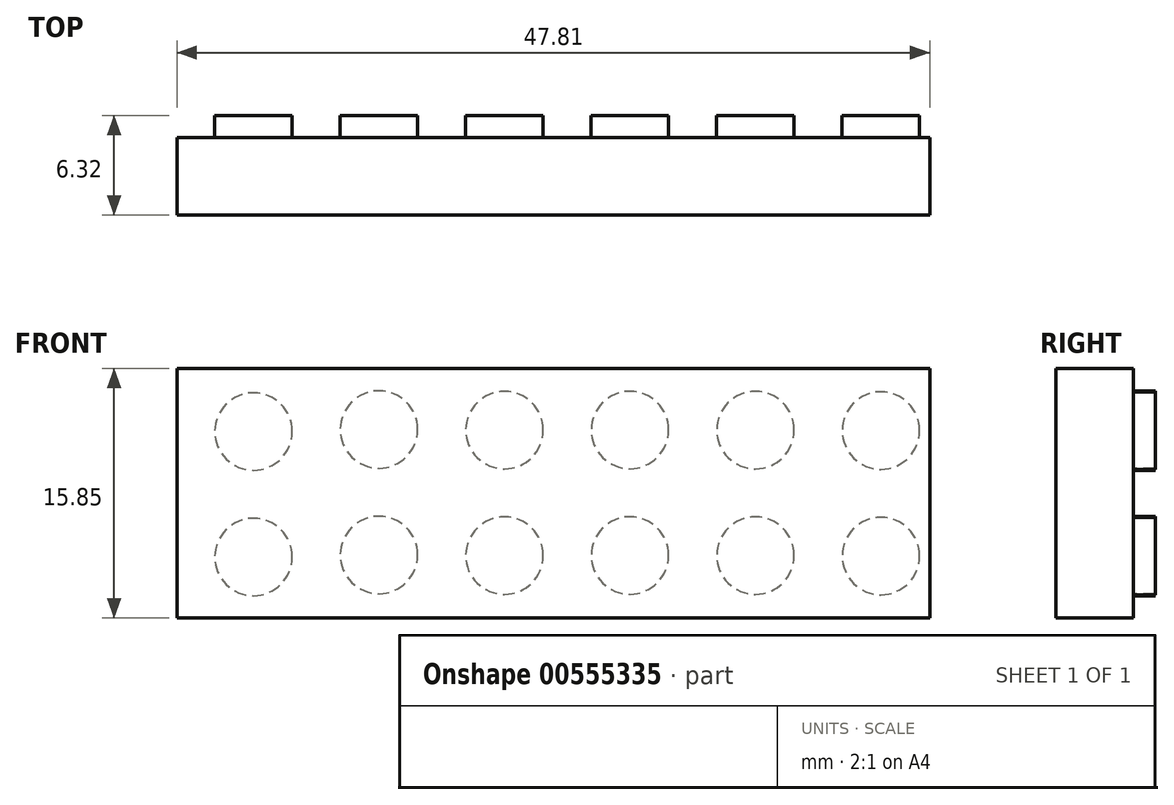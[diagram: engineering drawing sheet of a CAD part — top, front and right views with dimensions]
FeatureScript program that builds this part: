
annotation { "Feature Type Name" : "Feature", "Feature Type Description" : "" }
export const myFeature = defineFeature(function(context is Context, id is Id, definition is map)
    precondition{}
    {
        {
            var Q0;
            Q0=qCreatedBy(makeId("Front.planeOp"),FACE);
            var sketch = newSketch(context, id + "F0", { "sketchPlane" : qUnion([Q0])});
            skLineSegment(sketch, "E0.bottom", {"start": v(0, 0) * mm, "end": v(-47.81, 0) * mm});
            skLineSegment(sketch, "E0.top", {"start": v(0, 15.85) * mm, "end": v(-47.81, 15.85) * mm});
            skLineSegment(sketch, "E0.left", {"start": v(0, 0) * mm, "end": v(0, 15.85) * mm});
            skLineSegment(sketch, "E0.right", {"start": v(-47.81, 0) * mm, "end": v(-47.81, 15.85) * mm});
            skCircle(sketch, "E1", {"center": v(-43.4, 10.92) * mm, "radius": 2.46 * mm});
            skCircle(sketch, "E2", {"center": v(-45.35, 4.6) * mm, "radius": 2.46 * mm});
            skCircle(sketch, "E3", {"center": v(-34.78, 10.92) * mm, "radius": 2.46 * mm});
            skCircle(sketch, "E4", {"center": v(-40.43, 4.77) * mm, "radius": 2.46 * mm});
            skCircle(sketch, "E5", {"center": v(-26.73, 10.92) * mm, "radius": 2.46 * mm});
            skCircle(sketch, "E6", {"center": v(-26.73, 5.17) * mm, "radius": 2.46 * mm});
            skCircle(sketch, "E7", {"center": v(-21.81, 10.69) * mm, "radius": 2.46 * mm});
            skCircle(sketch, "E8", {"center": v(-20.12, 3.16) * mm, "radius": 2.46 * mm});
            skCircle(sketch, "E9", {"center": v(-13.22, 10.92) * mm, "radius": 2.46 * mm});
            skCircle(sketch, "E10", {"center": v(-13.8, 3.16) * mm, "radius": 2.46 * mm});
            skCircle(sketch, "E11", {"center": v(-6.32, 10.92) * mm, "radius": 2.46 * mm});
            skCircle(sketch, "E12", {"center": v(-8.88, 3.16) * mm, "radius": 2.46 * mm});
            skSolve(sketch);
        }
        {
            var Q0;
            {var subQ0=sQuery(id+"F0.wireOp",EDGE,"E2");var subQ1=makeQuery(id+"F0.imprint","INTERSECT",VERTEX,{"derivedFrom":[sQuery(id+"F0.wireOp",EDGE,"E0.right"),subQ0]});Q0=makeQuery(id+"F0.imprint","IMPRINT",FACE,{"disambiguationData":[TD([[makeQuery(id+"F0.imprint","IMPRINT",EDGE,{"disambiguationData":[TD([[subQ1,1.0]])],"derivedFrom":subQ0}),1.0]])]});}
            var Q1;
            Q1=makeQuery(id+"F0.imprint","IMPRINT",FACE,{"disambiguationData":[TD([[makeQuery(id+"F0.imprint","IMPRINT",EDGE,{"derivedFrom":sQuery(id+"F0.wireOp",EDGE,"E4")}),1.0]])]});
            var Q2;
            Q2=makeQuery(id+"F0.imprint","IMPRINT",FACE,{"disambiguationData":[TD([[makeQuery(id+"F0.imprint","IMPRINT",EDGE,{"derivedFrom":sQuery(id+"F0.wireOp",EDGE,"E1")}),1.0]])]});
            var Q3;
            Q3=makeQuery(id+"F0.imprint","IMPRINT",FACE,{"disambiguationData":[TD([[makeQuery(id+"F0.imprint","IMPRINT",EDGE,{"derivedFrom":sQuery(id+"F0.wireOp",EDGE,"E6")}),1.0]])]});
            var Q4;
            Q4=makeQuery(id+"F0.imprint","IMPRINT",FACE,{"disambiguationData":[TD([[makeQuery(id+"F0.imprint","IMPRINT",EDGE,{"derivedFrom":sQuery(id+"F0.wireOp",EDGE,"E5")}),1.0]])]});
            var Q5;
            Q5=makeQuery(id+"F0.imprint","IMPRINT",FACE,{"disambiguationData":[TD([[makeQuery(id+"F0.imprint","IMPRINT",EDGE,{"derivedFrom":sQuery(id+"F0.wireOp",EDGE,"E7")}),1.0]])]});
            var Q6;
            Q6=makeQuery(id+"F0.imprint","IMPRINT",FACE,{"disambiguationData":[TD([[makeQuery(id+"F0.imprint","IMPRINT",EDGE,{"derivedFrom":sQuery(id+"F0.wireOp",EDGE,"E8")}),1.0]])]});
            var Q7;
            Q7=makeQuery(id+"F0.imprint","IMPRINT",FACE,{"disambiguationData":[TD([[makeQuery(id+"F0.imprint","IMPRINT",EDGE,{"derivedFrom":sQuery(id+"F0.wireOp",EDGE,"E10")}),1.0]])]});
            var Q8;
            Q8=makeQuery(id+"F0.imprint","IMPRINT",FACE,{"disambiguationData":[TD([[makeQuery(id+"F0.imprint","IMPRINT",EDGE,{"derivedFrom":sQuery(id+"F0.wireOp",EDGE,"E12")}),1.0]])]});
            var Q9;
            Q9=makeQuery(id+"F0.imprint","IMPRINT",FACE,{"disambiguationData":[TD([[makeQuery(id+"F0.imprint","IMPRINT",EDGE,{"derivedFrom":sQuery(id+"F0.wireOp",EDGE,"E9")}),1.0]])]});
            var Q10;
            Q10=makeQuery(id+"F0.imprint","IMPRINT",FACE,{"disambiguationData":[TD([[makeQuery(id+"F0.imprint","IMPRINT",EDGE,{"derivedFrom":sQuery(id+"F0.wireOp",EDGE,"E11")}),1.0]])]});
            var Q11;
            {var subQ6=sQuery(id+"F0.wireOp",EDGE,"E0.bottom");Q11=makeQuery(id+"F0.imprint","IMPRINT",FACE,{"disambiguationData":[TD([[makeQuery(id+"F0.imprint","IMPRINT",EDGE,{"derivedFrom":subQ6}),-1.0]])]});}
            var Q12;
            Q12=makeQuery(id+"F0.imprint","IMPRINT",FACE,{"disambiguationData":[TD([[makeQuery(id+"F0.imprint","IMPRINT",EDGE,{"derivedFrom":sQuery(id+"F0.wireOp",EDGE,"E3")}),1.0]])]});
            extrude(context, id + "F1", {"entities" : qUnion([Q0, Q1, Q2, Q3, Q4, Q5, Q6, Q7, Q8, Q9, Q10, Q11, Q12]), "depth" : 4.92 * mm, "offsetDistance" : 25 * mm});
        }
        {
            var Q0;
            Q0=qCreatedBy(makeId("Front.planeOp"),FACE);
            var sketch = newSketch(context, id + "F2", { "sketchPlane" : qUnion([Q0])});
            skCircle(sketch, "E13", {"center": v(-42.95, 11.84) * mm, "radius": 2.46 * mm});
            skCircle(sketch, "E14", {"center": v(-42.95, 3.88) * mm, "radius": 2.46 * mm});
            skCircle(sketch, "E15", {"center": v(-34.98, 11.98) * mm, "radius": 2.46 * mm});
            skCircle(sketch, "E16", {"center": v(-34.98, 4) * mm, "radius": 2.46 * mm});
            skCircle(sketch, "E17", {"center": v(-27.01, 11.93) * mm, "radius": 2.46 * mm});
            skCircle(sketch, "E18", {"center": v(-19.04, 11.94) * mm, "radius": 2.46 * mm});
            skCircle(sketch, "E19", {"center": v(-11.07, 3.97) * mm, "radius": 2.46 * mm});
            skCircle(sketch, "E20", {"center": v(-11.07, 11.94) * mm, "radius": 2.46 * mm});
            skCircle(sketch, "E21", {"center": v(-3.1, 3.94) * mm, "radius": 2.46 * mm});
            skCircle(sketch, "E22", {"center": v(-3.1, 11.9) * mm, "radius": 2.46 * mm});
            skCircle(sketch, "E23", {"center": v(-19.04, 3.97) * mm, "radius": 2.46 * mm});
            skCircle(sketch, "E24", {"center": v(-27.01, 3.96) * mm, "radius": 2.46 * mm});
            skSolve(sketch);
        }
        {
            var Q0;
            Q0=sQuery(id+"F2.wireOp",EDGE,"E16");
            var Q1;
            Q1=sQuery(id+"F2.wireOp",EDGE,"E15");
            var Q2;
            Q2=sQuery(id+"F2.wireOp",EDGE,"E13");
            var Q3;
            Q3=sQuery(id+"F2.wireOp",EDGE,"E14");
            var Q4;
            Q4=sQuery(id+"F2.wireOp",EDGE,"E24");
            var Q5;
            Q5=sQuery(id+"F2.wireOp",EDGE,"E17");
            var Q6;
            Q6=sQuery(id+"F2.wireOp",EDGE,"E18");
            var Q7;
            Q7=sQuery(id+"F2.wireOp",EDGE,"E23");
            var Q8;
            Q8=sQuery(id+"F2.wireOp",EDGE,"E19");
            var Q9;
            Q9=sQuery(id+"F2.wireOp",EDGE,"E20");
            var Q10;
            Q10=sQuery(id+"F2.wireOp",EDGE,"E21");
            var Q11;
            Q11=sQuery(id+"F2.wireOp",EDGE,"E22");
            extrude(context, id + "F3", {"bodyType" : ToolBodyType.SURFACE, "surfaceEntities" : qUnion([Q0, Q1, Q2, Q3, Q4, Q5, Q6, Q7, Q8, Q9, Q10, Q11]), "depth" : 1.93 * mm, "offsetDistance" : 25 * mm});
        }
        {
            var Q0;
            Q0 = qSketchRegion(id + "F2", true);
            extrude(context, id + "F4", {"entities" : qUnion([Q0]), "operationType" : NewBodyOperationType.ADD, "oppositeDirection" : true, "depth" : 1.4 * mm, "offsetDistance" : 25 * mm});
        }
    });
